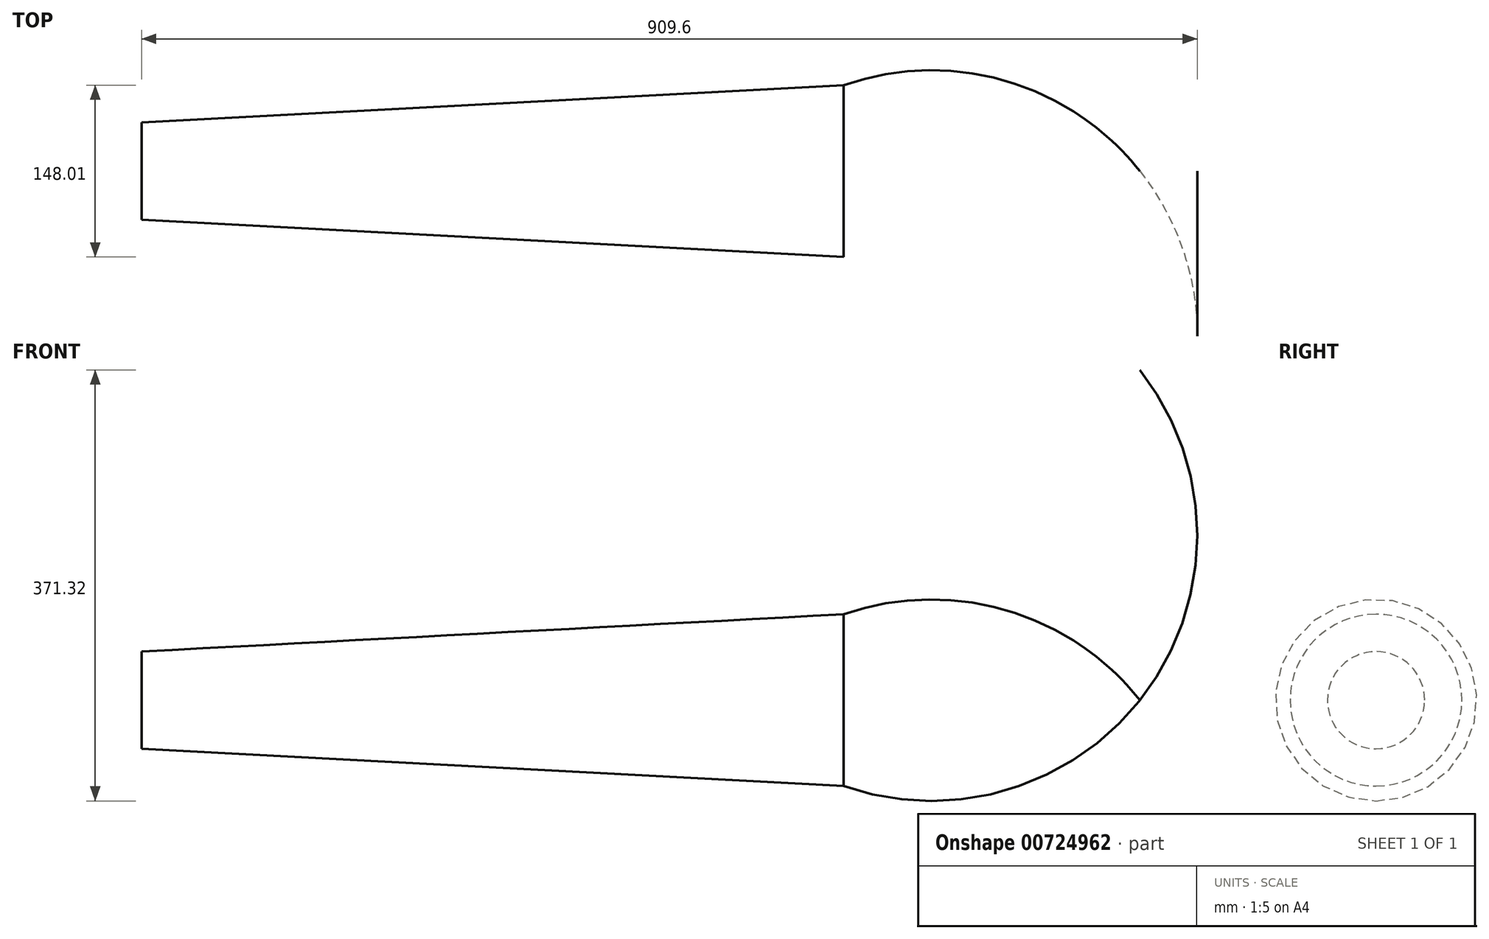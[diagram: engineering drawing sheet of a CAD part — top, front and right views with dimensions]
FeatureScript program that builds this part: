
annotation { "Feature Type Name" : "Feature", "Feature Type Description" : "" }
export const myFeature = defineFeature(function(context is Context, id is Id, definition is map)
    precondition{}
    {
        {
            var Q0;
            Q0=qCreatedBy(makeId("Top.planeOp"),FACE);
            var sketch = newSketch(context, id + "F0", { "sketchPlane" : qUnion([Q0])});
            skLineSegment(sketch, "E0", {"start": v(297.02, 42.86) * mm, "end": v(2528.7, 42.86) * mm});
            skLineSegment(sketch, "E1", {"start": v(297.02, 84.74) * mm, "end": v(297.02, 42.86) * mm});
            skArc(sketch, "E2", {"start": v(1157.1, 42.86) * mm, "mid": v(977.54, 129.7) * mm, "end": v(797.97, 42.86) * mm});
            skLineSegment(sketch, "E3", {"start": v(297.02, 84.74) * mm, "end": v(901.95, 116.87) * mm});
            skLineSegment(sketch, "E4", {"start": v(2528.7, 42.86) * mm, "end": v(2529.54, 91.37) * mm});
            skLineSegment(sketch, "E5", {"start": v(2529.54, 91.37) * mm, "end": v(1053.12, 116.87) * mm});
            skSolve(sketch);
        }
        {
            var Q0;
            {var subQ0=sQuery(id+"F0.wireOp",EDGE,"E2");var subQ1=sQuery(id+"F0.wireOp",EDGE,"E0");var subQ2=makeQuery(id+"F0.imprint","INTERSECT",VERTEX,{"disambiguationData":[OD(0.0)],"derivedFrom":[subQ1,subQ0]});Q0=makeQuery(id+"F0.imprint","IMPRINT",FACE,{"disambiguationData":[TD([[makeQuery(id+"F0.imprint","IMPRINT",EDGE,{"disambiguationData":[TD([[subQ2,1.0]])],"derivedFrom":subQ1}),1.0]])]});}
            var Q1;
            {var subQ0=sQuery(id+"F0.wireOp",EDGE,"E1");Q1=makeQuery(id+"F0.imprint","IMPRINT",FACE,{"disambiguationData":[TD([[makeQuery(id+"F0.imprint","IMPRINT",EDGE,{"derivedFrom":subQ0}),1.0]])]});}
            var Q2;
            {var subQ0=sQuery(id+"F0.wireOp",EDGE,"gvZ9CAlb-v8Dr-h7Jf-8ZLG-QRIv754dJV6o");Q2=makeQuery(id+"F0.imprint","IMPRINT",FACE,{"disambiguationData":[TD([[makeQuery(id+"F0.imprint","IMPRINT",EDGE,{"derivedFrom":subQ0}),-1.0]])]});}
            var Q3;
            Q3=sQuery(id+"F0.wireOp",EDGE,"E0");
            revolve(context, id + "F1", {"surfaceOperationType" : NewSurfaceOperationType.NEW, "entities" : qUnion([Q0, Q1, Q2]), "axis" : qUnion([Q3]), "revolveType" : RevolveType.FULL});
        }
    });
